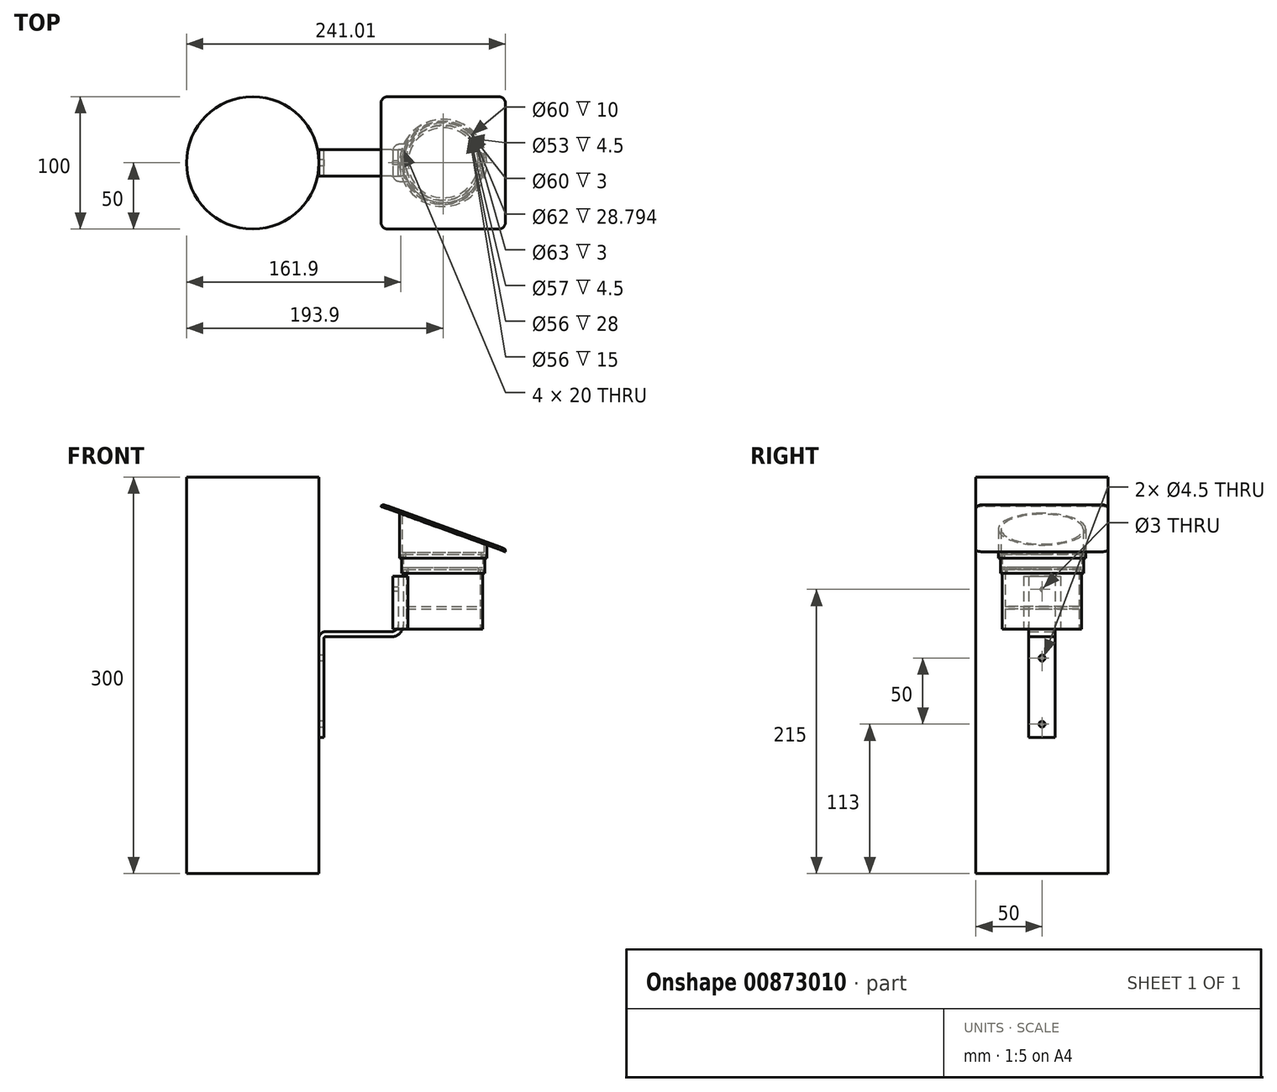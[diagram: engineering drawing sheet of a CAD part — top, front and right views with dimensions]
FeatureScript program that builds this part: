
annotation { "Feature Type Name" : "Feature", "Feature Type Description" : "" }
export const myFeature = defineFeature(function(context is Context, id is Id, definition is map)
    precondition{}
    {
        {
            var Q0;
            Q0=qCreatedBy(makeId("Front.planeOp"),FACE);
            var sketch = newSketch(context, id + "F0", { "sketchPlane" : qUnion([Q0])});
            skLineSegment(sketch, "E0", {"start": v(0, 0) * mm, "end": v(28, 0) * mm});
            skLineSegment(sketch, "E1", {"start": v(28, 0) * mm, "end": v(28, -15) * mm});
            skLineSegment(sketch, "E2", {"start": v(28, -15) * mm, "end": v(30, -15) * mm});
            skLineSegment(sketch, "E3", {"start": v(30, -15) * mm, "end": v(30, 30) * mm});
            skLineSegment(sketch, "E4", {"start": v(30, 30) * mm, "end": v(28, 30) * mm});
            skLineSegment(sketch, "E5", {"start": v(28, 30) * mm, "end": v(28, 2) * mm});
            skLineSegment(sketch, "E6", {"start": v(28, 2) * mm, "end": v(0, 2) * mm});
            skLineSegment(sketch, "E7", {"start": v(28, 27) * mm, "end": v(26.5, 27) * mm});
            skLineSegment(sketch, "E8", {"start": v(26.5, 27) * mm, "end": v(26.5, 31.5) * mm});
            skLineSegment(sketch, "E9", {"start": v(26.5, 31.5) * mm, "end": v(30, 31.5) * mm});
            skLineSegment(sketch, "E10", {"start": v(30, 31.5) * mm, "end": v(30, 41.5) * mm});
            skLineSegment(sketch, "E11", {"start": v(30, 41.5) * mm, "end": v(31.5, 41.5) * mm});
            skLineSegment(sketch, "E12", {"start": v(31.5, 41.5) * mm, "end": v(31.5, 27) * mm});
            skLineSegment(sketch, "E13", {"start": v(31.5, 27) * mm, "end": v(30, 27) * mm});
            skLineSegment(sketch, "E14", {"start": v(0, 0) * mm, "end": v(0, 2) * mm});
            skLineSegment(sketch, "E15", {"start": v(0, 0) * mm, "end": v(0, 68.73) * mm, "construction": true});
            skLineSegment(sketch, "E16", {"start": v(31.5, 38.5) * mm, "end": v(33, 38.5) * mm});
            skLineSegment(sketch, "E17", {"start": v(33, 38.5) * mm, "end": v(33, 81.5) * mm});
            skLineSegment(sketch, "E18", {"start": v(33, 81.5) * mm, "end": v(31, 81.5) * mm});
            skLineSegment(sketch, "E19", {"start": v(31, 81.5) * mm, "end": v(31, 43) * mm});
            skLineSegment(sketch, "E20", {"start": v(31, 43) * mm, "end": v(28.5, 43) * mm});
            skLineSegment(sketch, "E21", {"start": v(28.5, 43) * mm, "end": v(28.5, 38.5) * mm});
            skLineSegment(sketch, "E22", {"start": v(28.5, 38.5) * mm, "end": v(30, 38.5) * mm});
            skSolve(sketch);
        }
        {
            var Q0;
            Q0=makeQuery(id+"F0.imprint","IMPRINT",FACE,{"disambiguationData":[TD([[makeQuery(id+"F0.imprint","IMPRINT",EDGE,{"derivedFrom":sQuery(id+"F0.wireOp",EDGE,"E0")}),1.0]])]});
            var Q1;
            Q1=sQuery(id+"F0.wireOp",EDGE,"E15");
            revolve(context, id + "F1", {"surfaceOperationType" : NewSurfaceOperationType.NEW, "entities" : qUnion([Q0]), "axis" : qUnion([Q1]), "revolveType" : RevolveType.FULL});
        }
        {
            var Q0;
            {var subQ6=sQuery(id+"F0.wireOp",EDGE,"E4");Q0=makeQuery(id+"F0.imprint","IMPRINT",FACE,{"disambiguationData":[TD([[makeQuery(id+"F0.imprint","IMPRINT",EDGE,{"derivedFrom":subQ6}),-1.0]])]});}
            var Q1;
            Q1=sQuery(id+"F0.wireOp",EDGE,"E15");
            revolve(context, id + "F2", {"surfaceOperationType" : NewSurfaceOperationType.NEW, "entities" : qUnion([Q0]), "axis" : qUnion([Q1]), "revolveType" : RevolveType.FULL});
        }
        {
            var Q0;
            {var subQ1=sQuery(id+"F0.wireOp",EDGE,"E11");Q0=makeQuery(id+"F0.imprint","IMPRINT",FACE,{"disambiguationData":[TD([[makeQuery(id+"F0.imprint","IMPRINT",EDGE,{"derivedFrom":subQ1}),1.0]])]});}
            var Q1;
            Q1=sQuery(id+"F0.wireOp",EDGE,"E15");
            revolve(context, id + "F3", {"surfaceOperationType" : NewSurfaceOperationType.NEW, "entities" : qUnion([Q0]), "axis" : qUnion([Q1]), "revolveType" : RevolveType.FULL});
        }
        {
            var Q0;
            Q0=qCreatedBy(makeId("Front.planeOp"),FACE);
            var sketch = newSketch(context, id + "F4", { "sketchPlane" : qUnion([Q0])});
            skLineSegment(sketch, "E23", {"start": v(-40.62, 75.3) * mm, "end": v(33, 48.5) * mm});
            skLineSegment(sketch, "E24", {"start": v(33, 48.5) * mm, "end": v(33, 90.78) * mm});
            skLineSegment(sketch, "E25", {"start": v(33, 90.78) * mm, "end": v(-40.62, 90.78) * mm});
            skLineSegment(sketch, "E26", {"start": v(-40.62, 90.78) * mm, "end": v(-40.62, 75.3) * mm});
            skSolve(sketch);
        }
        {
            var Q0;
            Q0 = qSketchRegion(id + "F4", true);
            extrude(context, id + "F5", {"entities" : qUnion([Q0]), "operationType" : NewBodyOperationType.REMOVE, "endBound" : BoundingType.THROUGH_ALL, "depth" : 25 * mm, "offsetDistance" : 25 * mm, "hasSecondDirection" : true, "secondDirectionBound" : SecondDirectionBoundingType.THROUGH_ALL, "secondDirectionOppositeDirection" : true, "secondDirectionDepth" : 25 * mm});
        }
        {
            var Q0;
            Q0=makeQuery(id+"F5.boolean.opBoolean","COPY",FACE,{"derivedFrom":makeQuery(id+"F5.opExtrude","SWEPT_FACE",FACE,{"disambiguationData":[OSD([sQuery(id+"F4.wireOp",EDGE,"E23")])]})});
            var sketch = newSketch(context, id + "F6", { "sketchPlane" : qUnion([Q0])});
            skLineSegment(sketch, "E27.bottom", {"start": v(24.3, 50) * mm, "end": v(-65.7, 50) * mm});
            skLineSegment(sketch, "E27.top", {"start": v(24.3, -50) * mm, "end": v(-65.7, -50) * mm});
            skLineSegment(sketch, "E27.left", {"start": v(29.3, 45) * mm, "end": v(29.3, -45) * mm});
            skLineSegment(sketch, "E27.right", {"start": v(-70.7, 45) * mm, "end": v(-70.7, -45) * mm});
            skPoint(sketch, "E27.middle", {"position": v(-20.7, 0) * mm});
            skPoint(sketch, "E28.visualSharp", {"position": v(-70.7, 50) * mm});
            skArc(sketch, "E28.filletArc", {"start": v(-65.7, 50) * mm, "mid": v(-69.23, 48.54) * mm, "end": v(-70.7, 45) * mm});
            skPoint(sketch, "E29.visualSharp", {"position": v(29.3, 50) * mm});
            skArc(sketch, "E29.filletArc", {"start": v(29.3, 45) * mm, "mid": v(27.84, 48.54) * mm, "end": v(24.3, 50) * mm});
            skPoint(sketch, "E30.visualSharp", {"position": v(29.3, -50) * mm});
            skArc(sketch, "E30.filletArc", {"start": v(24.3, -50) * mm, "mid": v(27.84, -48.54) * mm, "end": v(29.3, -45) * mm});
            skPoint(sketch, "E31.visualSharp", {"position": v(-70.7, -50) * mm});
            skArc(sketch, "E31.filletArc", {"start": v(-70.7, -45) * mm, "mid": v(-69.23, -48.54) * mm, "end": v(-65.7, -50) * mm});
            skSolve(sketch);
        }
        {
            var Q0;
            Q0 = qSketchRegion(id + "F6", true);
            extrude(context, id + "F7", {"entities" : qUnion([Q0]), "depth" : 2 * mm, "offsetDistance" : 25 * mm});
        }
        {
            var Q0;
            Q0=makeQuery(id+"F1.opRevolve","SWEPT_FACE",FACE,{"disambiguationData":[OSD([sQuery(id+"F0.wireOp",EDGE,"E2")])]});
            var sketch = newSketch(context, id + "F8", { "sketchPlane" : qUnion([Q0])});
            skLineSegment(sketch, "E32", {"start": v(-30, 10) * mm, "end": v(-30, -10) * mm});
            skLineSegment(sketch, "E33", {"start": v(-26.53, -14) * mm, "end": v(-38, -14) * mm});
            skLineSegment(sketch, "E34", {"start": v(-38, -14) * mm, "end": v(-38, 14) * mm});
            skLineSegment(sketch, "E35", {"start": v(-38, 14) * mm, "end": v(-26.53, 14) * mm});
            skLineSegment(sketch, "E36", {"start": v(-30, 10) * mm, "end": v(-34, 10) * mm});
            skLineSegment(sketch, "E37", {"start": v(-34, 10) * mm, "end": v(-34, -10) * mm});
            skLineSegment(sketch, "E38", {"start": v(-34, -10) * mm, "end": v(-30, -10) * mm});
            skLineSegment(sketch, "E39", {"start": v(0, 0) * mm, "end": v(-38, 0) * mm, "construction": true});
            skLineSegment(sketch, "E40", {"start": v(-26.53, 14) * mm, "end": v(-29, 0) * mm});
            skLineSegment(sketch, "E41", {"start": v(-29, 0) * mm, "end": v(-26.53, -14) * mm});
            skSolve(sketch);
        }
        {
            var Q0;
            Q0 = qSketchRegion(id + "F8", true);
            extrude(context, id + "F9", {"entities" : qUnion([Q0]), "operationType" : NewBodyOperationType.ADD, "oppositeDirection" : true, "depth" : 40 * mm, "offsetDistance" : 25 * mm});
        }
        {
            var Q0;
            Q0=makeQuery(id+"F9.opExtrude","SWEPT_EDGE",EDGE,{"disambiguationData":[OSD([sQuery(id+"F0.wireOp",EDGE,"E2"),sQuery(id+"F0.wireOp",EDGE,"E3"),sQuery(id+"F8.wireOp",EDGE,"E33"),sQuery(id+"F8.wireOp",EDGE,"E41")])]});
            var Q1;
            Q1=makeQuery(id+"F9.opExtrude","SWEPT_EDGE",EDGE,{"disambiguationData":[OSD([sQuery(id+"F8.wireOp",EDGE,"E33"),sQuery(id+"F8.wireOp",EDGE,"E34")])]});
            var Q2;
            Q2=makeQuery(id+"F9.opExtrude","SWEPT_EDGE",EDGE,{"disambiguationData":[OSD([sQuery(id+"F8.wireOp",EDGE,"E34"),sQuery(id+"F8.wireOp",EDGE,"E35")])]});
            fillet(context, id + "F10", {"entities" : qUnion([Q0, Q1, Q2]), "radius" : 5 * mm, "tangentPropagation" : true, "allowEdgeOverflow" : false});
        }
        {
            var Q0;
            Q0=qCreatedBy(makeId("Front.planeOp"),FACE);
            var sketch = newSketch(context, id + "F11", { "sketchPlane" : qUnion([Q0])});
            skLineSegment(sketch, "E42", {"start": v(-33.9, 25) * mm, "end": v(-33.9, -12) * mm});
            skLineSegment(sketch, "E43", {"start": v(-38.9, -17) * mm, "end": v(-88.9, -17) * mm});
            skPoint(sketch, "E44.visualSharp", {"position": v(-33.9, -17) * mm});
            skArc(sketch, "E44.filletArc", {"start": v(-38.9, -17) * mm, "mid": v(-35.36, -15.54) * mm, "end": v(-33.9, -12) * mm});
            skLineSegment(sketch, "E45", {"start": v(-93.9, -22) * mm, "end": v(-93.9, -97) * mm});
            skPoint(sketch, "E46.visualSharp", {"position": v(-93.9, -17) * mm});
            skArc(sketch, "E46.filletArc", {"start": v(-88.9, -17) * mm, "mid": v(-92.44, -18.46) * mm, "end": v(-93.9, -22) * mm});
            skLineSegment(sketch, "E47.0", {"start": v(-90.1, -22) * mm, "end": v(-90.1, -97) * mm});
            skLineSegment(sketch, "E47.1", {"start": v(-30.1, 25) * mm, "end": v(-30.1, -12) * mm});
            skArc(sketch, "E47.2", {"start": v(-38.9, -20.8) * mm, "mid": v(-32.68, -18.22) * mm, "end": v(-30.1, -12) * mm});
            skLineSegment(sketch, "E47.3", {"start": v(-38.9, -20.8) * mm, "end": v(-88.9, -20.8) * mm});
            skArc(sketch, "E47.4", {"start": v(-88.9, -20.8) * mm, "mid": v(-89.75, -21.15) * mm, "end": v(-90.1, -22) * mm});
            skLineSegment(sketch, "E48", {"start": v(-90.1, -97) * mm, "end": v(-93.9, -97) * mm});
            skLineSegment(sketch, "E49", {"start": v(-30.1, 25) * mm, "end": v(-33.9, 25) * mm});
            skSolve(sketch);
        }
        {
            var Q0;
            Q0 = qSketchRegion(id + "F11", true);
            extrude(context, id + "F12", {"entities" : qUnion([Q0]), "endBound" : BoundingType.SYMMETRIC, "depth" : 20 * mm, "offsetDistance" : 25 * mm});
        }
        {
            var Q0;
            Q0=makeQuery(id+"F12.opExtrude","SWEPT_FACE",FACE,{"disambiguationData":[OSD([sQuery(id+"F11.wireOp",EDGE,"E45")])]});
            var sketch = newSketch(context, id + "F13", { "sketchPlane" : qUnion([Q0])});
            skCircle(sketch, "E50", {"center": v(0, -87) * mm, "radius": 2.25 * mm});
            skCircle(sketch, "E51", {"center": v(0, -37) * mm, "radius": 2.25 * mm});
            skLineSegment(sketch, "E52", {"start": v(0, -37) * mm, "end": v(0, -97) * mm, "construction": true});
            skSolve(sketch);
        }
        {
            var Q0;
            Q0 = qSketchRegion(id + "F13", true);
            extrude(context, id + "F14", {"entities" : qUnion([Q0]), "operationType" : NewBodyOperationType.REMOVE, "endBound" : BoundingType.THROUGH_ALL, "oppositeDirection" : true, "depth" : 25 * mm, "offsetDistance" : 25 * mm});
        }
        {
            var Q0;
            Q0=makeQuery(id+"F9.opExtrude","SWEPT_FACE",FACE,{"disambiguationData":[OSD([sQuery(id+"F8.wireOp",EDGE,"E34")])]});
            var sketch = newSketch(context, id + "F15", { "sketchPlane" : qUnion([Q0])});
            skCircle(sketch, "E53", {"center": v(0, 15) * mm, "radius": 1.5 * mm});
            skSolve(sketch);
        }
        {
            var Q0;
            Q0 = qSketchRegion(id + "F15", true);
            extrude(context, id + "F16", {"entities" : qUnion([Q0]), "operationType" : NewBodyOperationType.REMOVE, "endBound" : BoundingType.UP_TO_NEXT, "oppositeDirection" : true, "depth" : 25 * mm, "offsetDistance" : 25 * mm});
        }
        {
            var Q0;
            Q0=makeQuery(id+"F7.opExtrude","CAP_FACE",FACE,{"disambiguationData":[OSD([sQuery(id+"F6.wireOp",EDGE,"E27.bottom"),sQuery(id+"F6.wireOp",EDGE,"E27.top"),sQuery(id+"F6.wireOp",EDGE,"E27.left"),sQuery(id+"F6.wireOp",EDGE,"E27.right"),sQuery(id+"F6.wireOp",EDGE,"E28.filletArc"),sQuery(id+"F6.wireOp",EDGE,"E29.filletArc"),sQuery(id+"F6.wireOp",EDGE,"E30.filletArc"),sQuery(id+"F6.wireOp",EDGE,"E31.filletArc")])],"isStart":false});
            fillet(context, id + "F17", {"entities" : qUnion([Q0]), "radius" : 2 * mm, "tangentPropagation" : true, "allowEdgeOverflow" : false});
        }
        {
            var Q0;
            Q0=qCreatedBy(makeId("Top.planeOp"),FACE);
            var sketch = newSketch(context, id + "F18", { "sketchPlane" : qUnion([Q0])});
            skCircle(sketch, "E54", {"center": v(-143.9, 0) * mm, "radius": 50 * mm});
            skPoint(sketch, "E54.first.point", {"position": v(-93.9, 0) * mm});
            skPoint(sketch, "E54.second.point", {"position": v(-193.63, -5.17) * mm});
            skPoint(sketch, "E54.third.point", {"position": v(-150.2, 49.6) * mm});
            skSolve(sketch);
        }
        {
            var Q0;
            Q0 = qSketchRegion(id + "F18", true);
            extrude(context, id + "F19", {"entities" : qUnion([Q0]), "operationType" : NewBodyOperationType.ADD, "depth" : 100 * mm, "offsetDistance" : 25 * mm, "hasSecondDirection" : true, "secondDirectionOppositeDirection" : true, "secondDirectionDepth" : 200 * mm});
        }
    });
